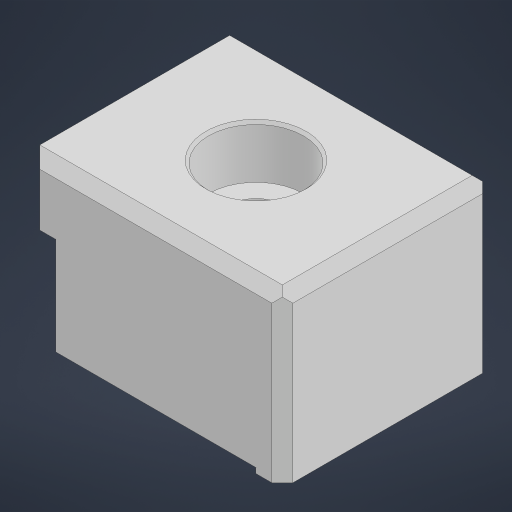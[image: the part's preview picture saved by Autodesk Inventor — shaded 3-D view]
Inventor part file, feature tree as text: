
AUTODESK INVENTOR PART (.ipt)
format: ipt  version: 2024.3 (Build 283343000, 343)  size: 192,000 bytes
history: native  units: mm
features: chamfer x4, sketch x2, extrude x1, hole x1, projected_geometry x1
ambient origin geometry x8: Origin, YZ Plane, XZ Plane, XY Plane, X Axis, Y Axis, Z Axis, Center Point
bodies: Solid1 (feature_tree)
feature tree (9):
  extrude  "Extrusion1"  Depth=31.5mm
  hole  "Hole1"  [1 undecoded]
  chamfer  "Chamfer1"  Distance=5.0mm
  chamfer  "Chamfer2"  Distance=40.0mm
  chamfer  "Chamfer3"  Distance=2.0mm Angle=45.0deg
  chamfer  "Chamfer4"  Distance=2.0mm Angle=45.0deg
  sketch  "Sketch1"  dims[d0=50.0mm d1=31.5mm]
  sketch  "Sketch2"  dims[d2=1.0mm d3=7.0mm d5=5.0mm d6=40.0mm d7=0.0mm d8=10.5mm d9=6.0mm d10=18.0mm d11=10.0mm d12=90.0deg d13=8.0mm d14=20.594885mm d15=2.0mm d16=2.0mm d17=45.0deg d18=4.0mm d19=2.0mm d20=45.0deg d23=18.0mm d24=12.0mm d25=19.5mm d26=38.0mm d27=0.5mm d28=2.0mm d29=45.0deg d30=0.5mm d31=2.0mm d32=45.0deg]
  projected_geometry  "Projected Loop1"
note: 1 required parameter value undecoded (feature->parameter linkage not recoverable at this tier; creation-order binding heuristic only, values carry confidence <= 0.55)
